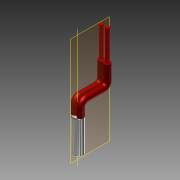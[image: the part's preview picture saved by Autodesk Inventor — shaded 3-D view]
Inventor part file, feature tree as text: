
AUTODESK INVENTOR PART (.ipt)
format: ipt  version: 2015 (Build 190159000, 159)  size: 132,608 bytes
history: native  units: mm
features: extrude x2, chamfer x1, sweep x1, other x1, projected_geometry x1
ambient origin geometry x8: Origin, YZ Plane, XZ Plane, XY Plane, X Axis, Y Axis, Z Axis, Center Point
bodies: Solid1 (feature_tree)
feature tree (6):
  extrude  "Extrusión1"  Depth=6.0mm
  chamfer  "Chaflán1"  Distance=20.0mm
  sweep  "Barrido1"
  extrude  "Extrusión2"  Depth=16.0mm
  other  "Eje de trabajo1"
  projected_geometry  "Contorno proyectado1"
